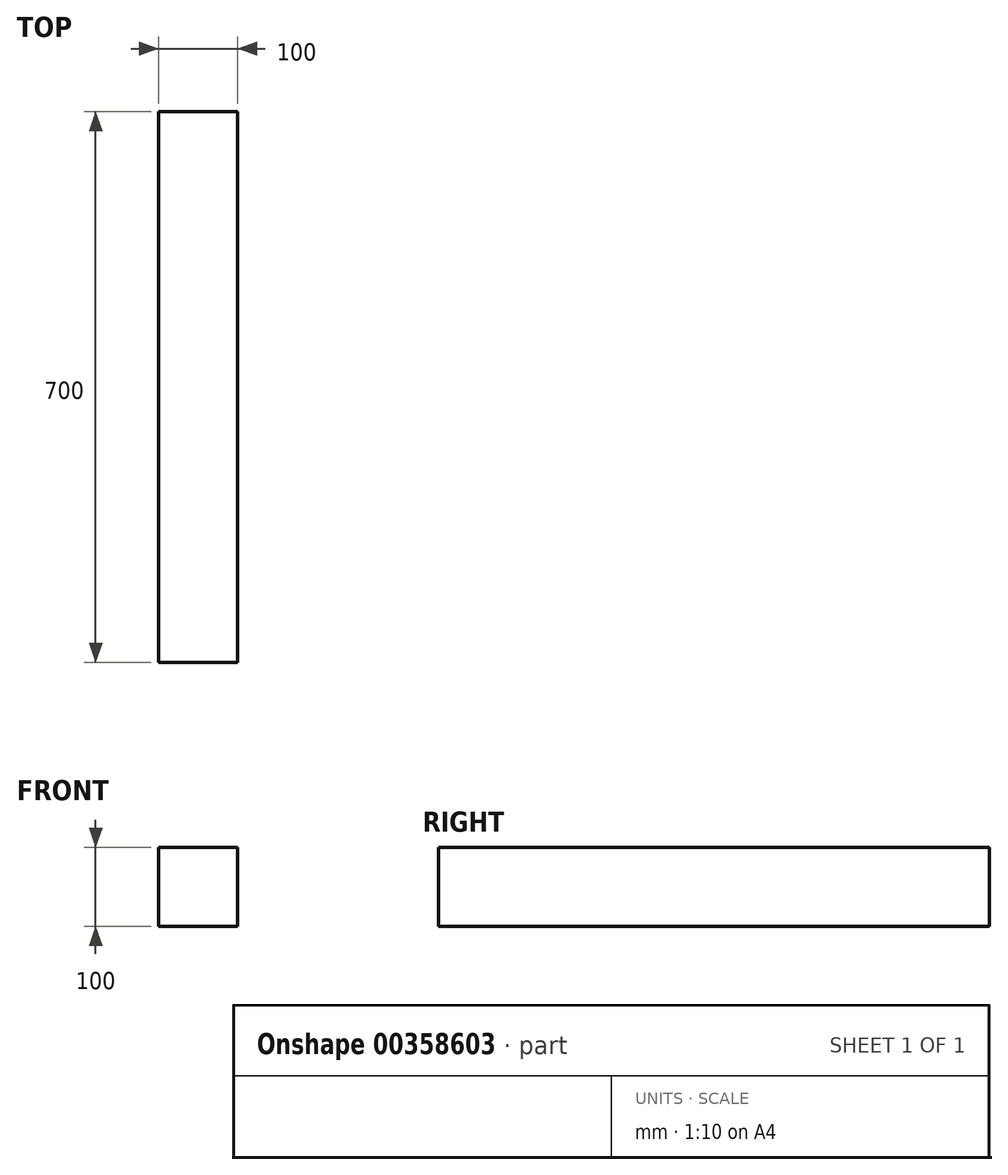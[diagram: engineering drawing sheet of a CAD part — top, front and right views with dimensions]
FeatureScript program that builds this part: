
annotation { "Feature Type Name" : "Feature", "Feature Type Description" : "" }
export const myFeature = defineFeature(function(context is Context, id is Id, definition is map)
    precondition{}
    {
        {
            var Q0;
            Q0=qCreatedBy(makeId("Front.planeOp"),FACE);
            var sketch = newSketch(context, id + "F0", { "sketchPlane" : qUnion([Q0])});
            skLineSegment(sketch, "E0.bottom", {"start": v(50, -50) * mm, "end": v(-50, -50) * mm});
            skLineSegment(sketch, "E0.top", {"start": v(50, 50) * mm, "end": v(-50, 50) * mm});
            skLineSegment(sketch, "E0.left", {"start": v(50, -50) * mm, "end": v(50, 50) * mm});
            skLineSegment(sketch, "E0.right", {"start": v(-50, -50) * mm, "end": v(-50, 50) * mm});
            skPoint(sketch, "E0.middle", {"position": v(0, 0) * mm});
            skSolve(sketch);
        }
        {
            var Q0;
            Q0 = qSketchRegion(id + "F0", true);
            extrude(context, id + "F1", {"entities" : qUnion([Q0]), "oppositeDirection" : true, "depth" : 700 * mm});
        }
    });
